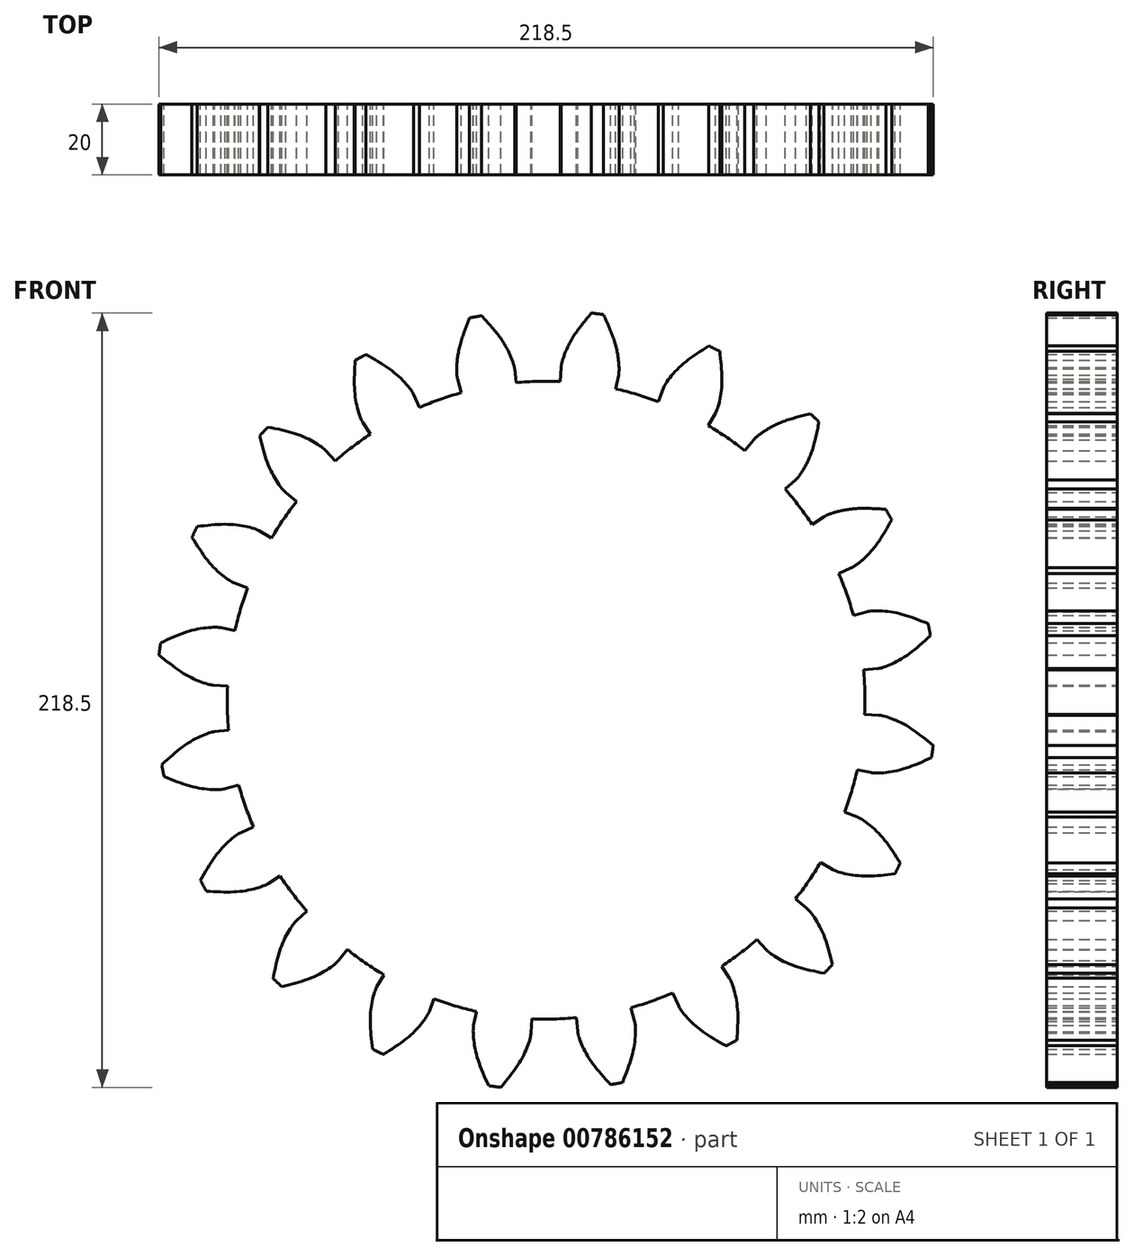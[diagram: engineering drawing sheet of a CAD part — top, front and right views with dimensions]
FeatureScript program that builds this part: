
annotation { "Feature Type Name" : "Feature", "Feature Type Description" : "" }
export const myFeature = defineFeature(function(context is Context, id is Id, definition is map)
    precondition{}
    {
        {
            var Q0;
            Q0=qCreatedBy(makeId("Front.planeOp"),FACE);
            var sketch = newSketch(context, id + "F0", { "sketchPlane" : qUnion([Q0])});
            skArc(sketch, "E0.0", {"start": v(-18.22, 108.48) * mm, "mid": v(-19.9, 108.18) * mm, "end": v(-21.6, 107.86) * mm});
            skCircle(sketch, "E1.0", {"center": v(0, 0) * mm, "radius": 90 * mm});
            skFitSpline(sketch, "E2", {"points": [v(-25, 90.58) * mm, v(-25.17, 91.74) * mm, v(-25.16, 95.16) * mm, v(-24.19, 100.64) * mm, v(-21.6, 107.86) * mm], "startDerivative": vector(-1.48, 7.52) * mm, "endDerivative": vector(8.54, 21.5) * mm});
            skLineSegment(sketch, "E3", {"start": v(-23.94, 86.76) * mm, "end": v(-25, 90.58) * mm});
            skLineSegment(sketch, "E4", {"start": v(-19.9, 108.18) * mm, "end": v(0, 0) * mm});
            skFitSpline(sketch, "E5.MirrorCS", {"points": [v(-8.89, 93.55) * mm, v(-9.14, 94.7) * mm, v(-10.37, 97.88) * mm, v(-13.22, 102.66) * mm, v(-18.22, 108.48) * mm], "startDerivative": vector(-1.3, 7.55) * mm, "endDerivative": vector(-15.63, 17.06) * mm});
            skLineSegment(sketch, "E6.MirrorCS", {"start": v(-8.51, 89.6) * mm, "end": v(-8.89, 93.55) * mm});
            skLineSegment(sketch, "E7.1.0", {"start": v(-52.36, 96.74) * mm, "end": v(0, 0) * mm});
            skLineSegment(sketch, "E7.2.0", {"start": v(-79.7, 75.82) * mm, "end": v(0, 0) * mm});
            skLineSegment(sketch, "E7.3.0", {"start": v(-99.22, 47.48) * mm, "end": v(0, 0) * mm});
            skLineSegment(sketch, "E7.4.0", {"start": v(-109.04, 14.5) * mm, "end": v(0, 0) * mm});
            skLineSegment(sketch, "E7.5.0", {"start": v(-108.18, -19.9) * mm, "end": v(0, 0) * mm});
            skLineSegment(sketch, "E7.6.0", {"start": v(-96.74, -52.36) * mm, "end": v(0, 0) * mm});
            skLineSegment(sketch, "E7.7.0", {"start": v(-75.82, -79.7) * mm, "end": v(0, 0) * mm});
            skLineSegment(sketch, "E7.8.0", {"start": v(-47.48, -99.22) * mm, "end": v(0, 0) * mm});
            skLineSegment(sketch, "E7.9.0", {"start": v(-14.5, -109.04) * mm, "end": v(0, 0) * mm});
            skLineSegment(sketch, "E7.10.0", {"start": v(19.9, -108.18) * mm, "end": v(0, 0) * mm});
            skLineSegment(sketch, "E7.11.0", {"start": v(52.36, -96.74) * mm, "end": v(0, 0) * mm});
            skLineSegment(sketch, "E7.12.0", {"start": v(79.7, -75.82) * mm, "end": v(0, 0) * mm});
            skLineSegment(sketch, "E7.13.0", {"start": v(99.22, -47.48) * mm, "end": v(0, 0) * mm});
            skLineSegment(sketch, "E7.14.0", {"start": v(109.04, -14.5) * mm, "end": v(0, 0) * mm});
            skLineSegment(sketch, "E7.15.0", {"start": v(108.18, 19.9) * mm, "end": v(0, 0) * mm});
            skLineSegment(sketch, "E7.16.0", {"start": v(96.74, 52.36) * mm, "end": v(0, 0) * mm});
            skLineSegment(sketch, "E7.17.0", {"start": v(75.82, 79.7) * mm, "end": v(0, 0) * mm});
            skLineSegment(sketch, "E7.18.0", {"start": v(47.48, 99.22) * mm, "end": v(0, 0) * mm});
            skLineSegment(sketch, "E7.19.0", {"start": v(14.5, 109.04) * mm, "end": v(0, 0) * mm});
            skArc(sketch, "E8.trimOffspring", {"start": v(-11.13, 99.38) * mm, "mid": v(-18.1, 98.35) * mm, "end": v(-24.98, 96.83) * mm});
            skLineSegment(sketch, "E9", {"start": v(-2.1, 84.34) * mm, "end": v(0, 0) * mm, "construction": true});
            skLineSegment(sketch, "E10.1.0", {"start": v(-28.06, 79.56) * mm, "end": v(0, 0) * mm, "construction": true});
            skLineSegment(sketch, "E10.2.0", {"start": v(-51.27, 67) * mm, "end": v(0, 0) * mm, "construction": true});
            skLineSegment(sketch, "E10.3.0", {"start": v(-69.47, 47.87) * mm, "end": v(0, 0) * mm, "construction": true});
            skLineSegment(sketch, "E10.4.0", {"start": v(-80.86, 24.06) * mm, "end": v(0, 0) * mm, "construction": true});
            skLineSegment(sketch, "E10.5.0", {"start": v(-84.34, -2.1) * mm, "end": v(0, 0) * mm, "construction": true});
            skLineSegment(sketch, "E10.6.0", {"start": v(-79.56, -28.06) * mm, "end": v(0, 0) * mm, "construction": true});
            skLineSegment(sketch, "E10.7.0", {"start": v(-67, -51.27) * mm, "end": v(0, 0) * mm, "construction": true});
            skLineSegment(sketch, "E10.8.0", {"start": v(-47.87, -69.47) * mm, "end": v(0, 0) * mm, "construction": true});
            skLineSegment(sketch, "E10.9.0", {"start": v(-24.06, -80.86) * mm, "end": v(0, 0) * mm, "construction": true});
            skLineSegment(sketch, "E10.10.0", {"start": v(2.1, -84.34) * mm, "end": v(0, 0) * mm, "construction": true});
            skLineSegment(sketch, "E10.11.0", {"start": v(28.06, -79.56) * mm, "end": v(0, 0) * mm, "construction": true});
            skLineSegment(sketch, "E10.12.0", {"start": v(51.27, -67) * mm, "end": v(0, 0) * mm, "construction": true});
            skLineSegment(sketch, "E10.13.0", {"start": v(69.47, -47.87) * mm, "end": v(0, 0) * mm, "construction": true});
            skLineSegment(sketch, "E10.14.0", {"start": v(80.86, -24.06) * mm, "end": v(0, 0) * mm, "construction": true});
            skLineSegment(sketch, "E10.15.0", {"start": v(84.34, 2.1) * mm, "end": v(0, 0) * mm, "construction": true});
            skLineSegment(sketch, "E10.16.0", {"start": v(79.56, 28.06) * mm, "end": v(0, 0) * mm, "construction": true});
            skLineSegment(sketch, "E10.17.0", {"start": v(67, 51.27) * mm, "end": v(0, 0) * mm, "construction": true});
            skLineSegment(sketch, "E10.18.0", {"start": v(47.87, 69.47) * mm, "end": v(0, 0) * mm, "construction": true});
            skLineSegment(sketch, "E10.19.0", {"start": v(24.06, 80.86) * mm, "end": v(0, 0) * mm, "construction": true});
            skLineSegment(sketch, "E11.MirrorCS", {"start": v(4.04, 89.9) * mm, "end": v(4.22, 93.87) * mm});
            skArc(sketch, "E12.MirrorCS", {"start": v(6.17, 99.8) * mm, "mid": v(13.18, 99.13) * mm, "end": v(20.13, 97.95) * mm});
            skFitSpline(sketch, "E13.MirrorCS", {"points": [v(4.22, 93.87) * mm, v(4.4, 95.03) * mm, v(5.48, 98.27) * mm, v(8.1, 103.19) * mm, v(12.8, 109.25) * mm], "startDerivative": vector(0.92, 7.6) * mm, "endDerivative": vector(14.76, 17.81) * mm});
            skArc(sketch, "E14.MirrorCS", {"start": v(12.8, 109.25) * mm, "mid": v(14.5, 109.04) * mm, "end": v(16.2, 108.8) * mm});
            skFitSpline(sketch, "E15.MirrorCS", {"points": [v(20.46, 91.72) * mm, v(20.57, 92.88) * mm, v(20.39, 96.3) * mm, v(19.15, 101.72) * mm, v(16.2, 108.8) * mm], "startDerivative": vector(1.1, 7.58) * mm, "endDerivative": vector(-9.6, 21.05) * mm});
            skLineSegment(sketch, "E16.MirrorCS", {"start": v(19.6, 87.84) * mm, "end": v(20.46, 91.72) * mm});
            skLineSegment(sketch, "E17.MirrorCS", {"start": v(31.63, 84.26) * mm, "end": v(33.02, 87.98) * mm});
            skFitSpline(sketch, "E18.MirrorCS", {"points": [v(33.02, 87.98) * mm, v(33.56, 89.02) * mm, v(35.58, 91.77) * mm, v(39.59, 95.64) * mm, v(45.93, 99.95) * mm], "startDerivative": vector(3.22, 6.95) * mm, "endDerivative": vector(19.55, 12.38) * mm});
            skFitSpline(sketch, "E19.MirrorCS", {"points": [v(47.8, 80.9) * mm, v(48.27, 81.98) * mm, v(49.14, 85.28) * mm, v(49.64, 90.83) * mm, v(49.02, 98.47) * mm], "startDerivative": vector(3.4, 6.87) * mm, "endDerivative": vector(-2.62, 22.99) * mm});
            skLineSegment(sketch, "E20.MirrorCS", {"start": v(45.78, 77.49) * mm, "end": v(47.8, 80.9) * mm});
            skArc(sketch, "E21.MirrorCS", {"start": v(49.02, 98.47) * mm, "mid": v(47.48, 99.22) * mm, "end": v(45.93, 99.95) * mm});
            skArc(sketch, "E22.MirrorCS", {"start": v(63.65, 77.12) * mm, "mid": v(68.93, 72.45) * mm, "end": v(73.86, 67.42) * mm});
            skFitSpline(sketch, "E23.MirrorCS", {"points": [v(58.6, 73.47) * mm, v(59.42, 74.29) * mm, v(62.2, 76.28) * mm, v(67.2, 78.72) * mm, v(74.57, 80.87) * mm], "startDerivative": vector(5.21, 5.62) * mm, "endDerivative": vector(22.41, 5.73) * mm});
            skLineSegment(sketch, "E24.MirrorCS", {"start": v(56.12, 70.36) * mm, "end": v(58.6, 73.47) * mm});
            skArc(sketch, "E25.MirrorCS", {"start": v(74.57, 80.87) * mm, "mid": v(75.82, 79.7) * mm, "end": v(77.05, 78.5) * mm});
            skFitSpline(sketch, "E26.MirrorCS", {"points": [v(70.46, 62.18) * mm, v(71.24, 63.05) * mm, v(73.1, 65.92) * mm, v(75.28, 71.04) * mm, v(77.05, 78.5) * mm], "startDerivative": vector(5.35, 5.49) * mm, "endDerivative": vector(4.61, 22.67) * mm});
            skLineSegment(sketch, "E27.MirrorCS", {"start": v(67.48, 59.55) * mm, "end": v(70.46, 62.18) * mm});
            skFitSpline(sketch, "E28.MirrorCS", {"points": [v(86.22, 37.36) * mm, v(87.23, 37.95) * mm, v(89.88, 40.1) * mm, v(93.55, 44.3) * mm, v(97.54, 50.85) * mm], "startDerivative": vector(6.78, 3.56) * mm, "endDerivative": vector(11.4, 20.14) * mm});
            skFitSpline(sketch, "E29.MirrorCS", {"points": [v(78.43, 51.77) * mm, v(79.47, 52.29) * mm, v(82.73, 53.33) * mm, v(88.24, 54.1) * mm, v(95.9, 53.87) * mm], "startDerivative": vector(6.7, 3.73) * mm, "endDerivative": vector(23.09, -1.47) * mm});
            skArc(sketch, "E30.MirrorCS", {"start": v(97.54, 50.85) * mm, "mid": v(96.74, 52.36) * mm, "end": v(95.9, 53.87) * mm});
            skArc(sketch, "E31.MirrorCS", {"start": v(91.08, 41.3) * mm, "mid": v(87.94, 47.6) * mm, "end": v(84.37, 53.68) * mm});
            skLineSegment(sketch, "E32.MirrorCS", {"start": v(75.11, 49.58) * mm, "end": v(78.43, 51.77) * mm});
            skLineSegment(sketch, "E33.MirrorCS", {"start": v(82.58, 35.78) * mm, "end": v(86.22, 37.36) * mm});
            skFitSpline(sketch, "E34.MirrorCS", {"points": [v(90.58, 25) * mm, v(91.74, 25.17) * mm, v(95.16, 25.16) * mm, v(100.64, 24.19) * mm, v(107.86, 21.6) * mm], "startDerivative": vector(7.52, 1.48) * mm, "endDerivative": vector(21.5, -8.54) * mm});
            skLineSegment(sketch, "E35.MirrorCS", {"start": v(86.76, 23.94) * mm, "end": v(90.58, 25) * mm});
            skFitSpline(sketch, "E36.MirrorCS", {"points": [v(93.55, 8.89) * mm, v(94.7, 9.14) * mm, v(97.88, 10.37) * mm, v(102.66, 13.22) * mm, v(108.48, 18.22) * mm], "startDerivative": vector(7.55, 1.3) * mm, "endDerivative": vector(17.06, 15.63) * mm});
            skArc(sketch, "E37.MirrorCS", {"start": v(107.86, 21.6) * mm, "mid": v(108.18, 19.9) * mm, "end": v(108.48, 18.22) * mm});
            skLineSegment(sketch, "E38.MirrorCS", {"start": v(89.6, 8.51) * mm, "end": v(93.55, 8.89) * mm});
            skFitSpline(sketch, "E39.MirrorCS", {"points": [v(93.87, -4.22) * mm, v(95.03, -4.4) * mm, v(98.27, -5.48) * mm, v(103.19, -8.1) * mm, v(109.25, -12.8) * mm], "startDerivative": vector(7.6, -0.92) * mm, "endDerivative": vector(17.81, -14.76) * mm});
            skLineSegment(sketch, "E40.MirrorCS", {"start": v(89.9, -4.04) * mm, "end": v(93.87, -4.22) * mm});
            skArc(sketch, "E41.MirrorCS", {"start": v(108.8, -16.2) * mm, "mid": v(109.04, -14.5) * mm, "end": v(109.25, -12.8) * mm});
            skFitSpline(sketch, "E42.MirrorCS", {"points": [v(91.72, -20.46) * mm, v(92.88, -20.57) * mm, v(96.3, -20.39) * mm, v(101.72, -19.15) * mm, v(108.8, -16.2) * mm], "startDerivative": vector(7.58, -1.1) * mm, "endDerivative": vector(21.05, 9.6) * mm});
            skLineSegment(sketch, "E43.MirrorCS", {"start": v(87.84, -19.6) * mm, "end": v(91.72, -20.46) * mm});
            skFitSpline(sketch, "E44.MirrorCS", {"points": [v(87.98, -33.02) * mm, v(89.02, -33.56) * mm, v(91.77, -35.58) * mm, v(95.64, -39.59) * mm, v(99.95, -45.93) * mm], "startDerivative": vector(6.95, -3.22) * mm, "endDerivative": vector(12.38, -19.55) * mm});
            skLineSegment(sketch, "E45.MirrorCS", {"start": v(84.26, -31.63) * mm, "end": v(87.98, -33.02) * mm});
            skLineSegment(sketch, "E46.MirrorCS", {"start": v(77.49, -45.78) * mm, "end": v(80.9, -47.8) * mm});
            skFitSpline(sketch, "E47.MirrorCS", {"points": [v(80.9, -47.8) * mm, v(81.98, -48.27) * mm, v(85.28, -49.14) * mm, v(90.83, -49.64) * mm, v(98.47, -49.02) * mm], "startDerivative": vector(6.87, -3.4) * mm, "endDerivative": vector(22.99, 2.62) * mm});
            skArc(sketch, "E48.MirrorCS", {"start": v(99.95, -45.93) * mm, "mid": v(99.22, -47.48) * mm, "end": v(98.47, -49.02) * mm});
            skLineSegment(sketch, "E49.MirrorCS", {"start": v(70.36, -56.12) * mm, "end": v(73.47, -58.6) * mm});
            skFitSpline(sketch, "E50.MirrorCS", {"points": [v(73.47, -58.6) * mm, v(74.29, -59.42) * mm, v(76.28, -62.2) * mm, v(78.72, -67.2) * mm, v(80.87, -74.57) * mm], "startDerivative": vector(5.62, -5.21) * mm, "endDerivative": vector(5.73, -22.41) * mm});
            skArc(sketch, "E51.MirrorCS", {"start": v(78.5, -77.05) * mm, "mid": v(79.7, -75.82) * mm, "end": v(80.87, -74.57) * mm});
            skFitSpline(sketch, "E52.MirrorCS", {"points": [v(62.18, -70.46) * mm, v(63.05, -71.24) * mm, v(65.92, -73.1) * mm, v(71.04, -75.28) * mm, v(78.5, -77.05) * mm], "startDerivative": vector(5.49, -5.35) * mm, "endDerivative": vector(22.67, -4.61) * mm});
            skLineSegment(sketch, "E53.MirrorCS", {"start": v(59.55, -67.48) * mm, "end": v(62.18, -70.46) * mm});
            skLineSegment(sketch, "E54.MirrorCS", {"start": v(-86.76, -23.94) * mm, "end": v(-90.58, -25) * mm});
            skFitSpline(sketch, "E55.MirrorCS", {"points": [v(-90.58, -25) * mm, v(-91.74, -25.17) * mm, v(-95.16, -25.16) * mm, v(-100.64, -24.19) * mm, v(-107.86, -21.6) * mm], "startDerivative": vector(-7.52, -1.48) * mm, "endDerivative": vector(-21.5, 8.54) * mm});
            skLineSegment(sketch, "E56.MirrorCS", {"start": v(-89.6, -8.51) * mm, "end": v(-93.55, -8.89) * mm});
            skFitSpline(sketch, "E57.MirrorCS", {"points": [v(-93.55, -8.89) * mm, v(-94.7, -9.14) * mm, v(-97.88, -10.37) * mm, v(-102.66, -13.22) * mm, v(-108.48, -18.22) * mm], "startDerivative": vector(-7.55, -1.3) * mm, "endDerivative": vector(-17.06, -15.63) * mm});
            skArc(sketch, "E58.MirrorCS", {"start": v(-107.86, -21.6) * mm, "mid": v(-108.18, -19.9) * mm, "end": v(-108.48, -18.22) * mm});
            skLineSegment(sketch, "E59.MirrorCS", {"start": v(-75.11, -49.58) * mm, "end": v(-78.43, -51.77) * mm});
            skFitSpline(sketch, "E60.MirrorCS", {"points": [v(-78.43, -51.77) * mm, v(-79.47, -52.29) * mm, v(-82.73, -53.33) * mm, v(-88.24, -54.1) * mm, v(-95.9, -53.87) * mm], "startDerivative": vector(-6.7, -3.73) * mm, "endDerivative": vector(-23.09, 1.47) * mm});
            skLineSegment(sketch, "E61.MirrorCS", {"start": v(-82.58, -35.78) * mm, "end": v(-86.22, -37.36) * mm});
            skFitSpline(sketch, "E62.MirrorCS", {"points": [v(-86.22, -37.36) * mm, v(-87.23, -37.95) * mm, v(-89.88, -40.1) * mm, v(-93.55, -44.3) * mm, v(-97.54, -50.85) * mm], "startDerivative": vector(-6.78, -3.56) * mm, "endDerivative": vector(-11.4, -20.14) * mm});
            skArc(sketch, "E63.MirrorCS", {"start": v(-97.54, -50.85) * mm, "mid": v(-96.74, -52.36) * mm, "end": v(-95.9, -53.87) * mm});
            skLineSegment(sketch, "E64.MirrorCS", {"start": v(-67.48, -59.55) * mm, "end": v(-70.46, -62.18) * mm});
            skFitSpline(sketch, "E65.MirrorCS", {"points": [v(-70.46, -62.18) * mm, v(-71.24, -63.05) * mm, v(-73.1, -65.92) * mm, v(-75.28, -71.04) * mm, v(-77.05, -78.5) * mm], "startDerivative": vector(-5.35, -5.49) * mm, "endDerivative": vector(-4.61, -22.67) * mm});
            skFitSpline(sketch, "E66.MirrorCS", {"points": [v(-58.6, -73.47) * mm, v(-59.42, -74.29) * mm, v(-62.2, -76.28) * mm, v(-67.2, -78.72) * mm, v(-74.57, -80.87) * mm], "startDerivative": vector(-5.21, -5.62) * mm, "endDerivative": vector(-22.41, -5.73) * mm});
            skLineSegment(sketch, "E67.MirrorCS", {"start": v(-56.12, -70.36) * mm, "end": v(-58.6, -73.47) * mm});
            skArc(sketch, "E68.MirrorCS", {"start": v(-74.57, -80.87) * mm, "mid": v(-75.82, -79.7) * mm, "end": v(-77.05, -78.5) * mm});
            skFitSpline(sketch, "E69.MirrorCS", {"points": [v(-33.02, -87.98) * mm, v(-33.56, -89.02) * mm, v(-35.58, -91.77) * mm, v(-39.59, -95.64) * mm, v(-45.93, -99.95) * mm], "startDerivative": vector(-3.22, -6.95) * mm, "endDerivative": vector(-19.55, -12.38) * mm});
            skLineSegment(sketch, "E70.MirrorCS", {"start": v(-31.63, -84.26) * mm, "end": v(-33.02, -87.98) * mm});
            skLineSegment(sketch, "E71.MirrorCS", {"start": v(-45.78, -77.49) * mm, "end": v(-47.8, -80.9) * mm});
            skFitSpline(sketch, "E72.MirrorCS", {"points": [v(-47.8, -80.9) * mm, v(-48.27, -81.98) * mm, v(-49.14, -85.28) * mm, v(-49.64, -90.83) * mm, v(-49.02, -98.47) * mm], "startDerivative": vector(-3.4, -6.87) * mm, "endDerivative": vector(2.62, -22.99) * mm});
            skArc(sketch, "E73.MirrorCS", {"start": v(-49.02, -98.47) * mm, "mid": v(-47.48, -99.22) * mm, "end": v(-45.93, -99.95) * mm});
            skFitSpline(sketch, "E74.MirrorCS", {"points": [v(-4.22, -93.87) * mm, v(-4.4, -95.03) * mm, v(-5.48, -98.27) * mm, v(-8.1, -103.19) * mm, v(-12.8, -109.25) * mm], "startDerivative": vector(-0.92, -7.6) * mm, "endDerivative": vector(-14.76, -17.81) * mm});
            skLineSegment(sketch, "E75.MirrorCS", {"start": v(-4.04, -89.9) * mm, "end": v(-4.22, -93.87) * mm});
            skFitSpline(sketch, "E76.MirrorCS", {"points": [v(-20.46, -91.72) * mm, v(-20.57, -92.88) * mm, v(-20.39, -96.3) * mm, v(-19.15, -101.72) * mm, v(-16.2, -108.8) * mm], "startDerivative": vector(-1.1, -7.58) * mm, "endDerivative": vector(9.6, -21.05) * mm});
            skLineSegment(sketch, "E77.MirrorCS", {"start": v(-19.6, -87.84) * mm, "end": v(-20.46, -91.72) * mm});
            skArc(sketch, "E78.MirrorCS", {"start": v(-12.8, -109.25) * mm, "mid": v(-14.5, -109.04) * mm, "end": v(-16.2, -108.8) * mm});
            skFitSpline(sketch, "E79.MirrorCS", {"points": [v(8.89, -93.55) * mm, v(9.14, -94.7) * mm, v(10.37, -97.88) * mm, v(13.22, -102.66) * mm, v(18.22, -108.48) * mm], "startDerivative": vector(1.3, -7.55) * mm, "endDerivative": vector(15.63, -17.06) * mm});
            skLineSegment(sketch, "E80.MirrorCS", {"start": v(8.51, -89.6) * mm, "end": v(8.89, -93.55) * mm});
            skFitSpline(sketch, "E81.MirrorCS", {"points": [v(25, -90.58) * mm, v(25.17, -91.74) * mm, v(25.16, -95.16) * mm, v(24.19, -100.64) * mm, v(21.6, -107.86) * mm], "startDerivative": vector(1.48, -7.52) * mm, "endDerivative": vector(-8.54, -21.5) * mm});
            skLineSegment(sketch, "E82.MirrorCS", {"start": v(23.94, -86.76) * mm, "end": v(25, -90.58) * mm});
            skArc(sketch, "E83.MirrorCS", {"start": v(18.22, -108.48) * mm, "mid": v(19.9, -108.18) * mm, "end": v(21.6, -107.86) * mm});
            skLineSegment(sketch, "E84.MirrorCS", {"start": v(49.58, -75.11) * mm, "end": v(51.77, -78.43) * mm});
            skFitSpline(sketch, "E85.MirrorCS", {"points": [v(51.77, -78.43) * mm, v(52.29, -79.47) * mm, v(53.33, -82.73) * mm, v(54.1, -88.24) * mm, v(53.87, -95.9) * mm], "startDerivative": vector(3.73, -6.7) * mm, "endDerivative": vector(-1.47, -23.09) * mm});
            skArc(sketch, "E86.MirrorCS", {"start": v(53.87, -95.9) * mm, "mid": v(52.36, -96.74) * mm, "end": v(50.85, -97.54) * mm});
            skFitSpline(sketch, "E87.MirrorCS", {"points": [v(37.36, -86.22) * mm, v(37.95, -87.23) * mm, v(40.1, -89.88) * mm, v(44.3, -93.55) * mm, v(50.85, -97.54) * mm], "startDerivative": vector(3.56, -6.78) * mm, "endDerivative": vector(20.14, -11.4) * mm});
            skLineSegment(sketch, "E88.MirrorCS", {"start": v(35.78, -82.58) * mm, "end": v(37.36, -86.22) * mm});
            skLineSegment(sketch, "E89.MirrorCS", {"start": v(-35.78, 82.58) * mm, "end": v(-37.36, 86.22) * mm});
            skFitSpline(sketch, "E90.MirrorCS", {"points": [v(-37.36, 86.22) * mm, v(-37.95, 87.23) * mm, v(-40.1, 89.88) * mm, v(-44.3, 93.55) * mm, v(-50.85, 97.54) * mm], "startDerivative": vector(-3.56, 6.78) * mm, "endDerivative": vector(-20.14, 11.4) * mm});
            skFitSpline(sketch, "E91.MirrorCS", {"points": [v(-51.77, 78.43) * mm, v(-52.29, 79.47) * mm, v(-53.33, 82.73) * mm, v(-54.1, 88.24) * mm, v(-53.87, 95.9) * mm], "startDerivative": vector(-3.73, 6.7) * mm, "endDerivative": vector(1.47, 23.09) * mm});
            skLineSegment(sketch, "E92.MirrorCS", {"start": v(-49.58, 75.11) * mm, "end": v(-51.77, 78.43) * mm});
            skArc(sketch, "E93.MirrorCS", {"start": v(-53.87, 95.9) * mm, "mid": v(-52.36, 96.74) * mm, "end": v(-50.85, 97.54) * mm});
            skFitSpline(sketch, "E94.MirrorCS", {"points": [v(-62.18, 70.46) * mm, v(-63.05, 71.24) * mm, v(-65.92, 73.1) * mm, v(-71.04, 75.28) * mm, v(-78.5, 77.05) * mm], "startDerivative": vector(-5.49, 5.35) * mm, "endDerivative": vector(-22.67, 4.61) * mm});
            skLineSegment(sketch, "E95.MirrorCS", {"start": v(-59.55, 67.48) * mm, "end": v(-62.18, 70.46) * mm});
            skLineSegment(sketch, "E96.MirrorCS", {"start": v(-70.36, 56.12) * mm, "end": v(-73.47, 58.6) * mm});
            skFitSpline(sketch, "E97.MirrorCS", {"points": [v(-73.47, 58.6) * mm, v(-74.29, 59.42) * mm, v(-76.28, 62.2) * mm, v(-78.72, 67.2) * mm, v(-80.87, 74.57) * mm], "startDerivative": vector(-5.62, 5.21) * mm, "endDerivative": vector(-5.73, 22.41) * mm});
            skArc(sketch, "E98.MirrorCS", {"start": v(-78.5, 77.05) * mm, "mid": v(-79.7, 75.82) * mm, "end": v(-80.87, 74.57) * mm});
            skFitSpline(sketch, "E99.MirrorCS", {"points": [v(-80.9, 47.8) * mm, v(-81.98, 48.27) * mm, v(-85.28, 49.14) * mm, v(-90.83, 49.64) * mm, v(-98.47, 49.02) * mm], "startDerivative": vector(-6.87, 3.4) * mm, "endDerivative": vector(-22.99, -2.62) * mm});
            skLineSegment(sketch, "E100.MirrorCS", {"start": v(-77.49, 45.78) * mm, "end": v(-80.9, 47.8) * mm});
            skFitSpline(sketch, "E101.MirrorCS", {"points": [v(-87.98, 33.02) * mm, v(-89.02, 33.56) * mm, v(-91.77, 35.58) * mm, v(-95.64, 39.59) * mm, v(-99.95, 45.93) * mm], "startDerivative": vector(-6.95, 3.22) * mm, "endDerivative": vector(-12.38, 19.55) * mm});
            skLineSegment(sketch, "E102.MirrorCS", {"start": v(-84.26, 31.63) * mm, "end": v(-87.98, 33.02) * mm});
            skArc(sketch, "E103.MirrorCS", {"start": v(-99.95, 45.93) * mm, "mid": v(-99.22, 47.48) * mm, "end": v(-98.47, 49.02) * mm});
            skFitSpline(sketch, "E104.MirrorCS", {"points": [v(-93.87, 4.22) * mm, v(-95.03, 4.4) * mm, v(-98.27, 5.48) * mm, v(-103.19, 8.1) * mm, v(-109.25, 12.8) * mm], "startDerivative": vector(-7.6, 0.92) * mm, "endDerivative": vector(-17.81, 14.76) * mm});
            skLineSegment(sketch, "E105.MirrorCS", {"start": v(-89.9, 4.04) * mm, "end": v(-93.87, 4.22) * mm});
            skLineSegment(sketch, "E106.MirrorCS", {"start": v(-87.84, 19.6) * mm, "end": v(-91.72, 20.46) * mm});
            skFitSpline(sketch, "E107.MirrorCS", {"points": [v(-91.72, 20.46) * mm, v(-92.88, 20.57) * mm, v(-96.3, 20.39) * mm, v(-101.72, 19.15) * mm, v(-108.8, 16.2) * mm], "startDerivative": vector(-7.58, 1.1) * mm, "endDerivative": vector(-21.05, -9.6) * mm});
            skArc(sketch, "E108.MirrorCS", {"start": v(-108.8, 16.2) * mm, "mid": v(-109.04, 14.5) * mm, "end": v(-109.25, 12.8) * mm});
            skFitSpline(sketch, "E109.MirrorCS", {"points": [v(-93.87, 4.22) * mm, v(-95.03, 4.4) * mm, v(-98.27, 5.48) * mm, v(-103.19, 8.1) * mm, v(-109.25, 12.8) * mm], "startDerivative": vector(-7.6, 0.92) * mm, "endDerivative": vector(-17.81, 14.76) * mm});
            skSolve(sketch);
        }
        {
            var Q0;
            Q0 = qSketchRegion(id + "F0", true);
            extrude(context, id + "F1", {"entities" : qUnion([Q0]), "endBound" : BoundingType.SYMMETRIC, "depth" : 20 * mm, "offsetDistance" : 25.4 * mm});
        }
    });
